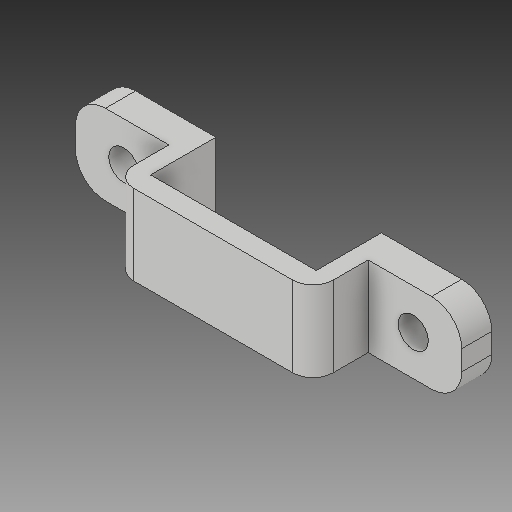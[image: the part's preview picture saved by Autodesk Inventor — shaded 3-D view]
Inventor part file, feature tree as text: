
AUTODESK INVENTOR PART (.ipt)
format: ipt  version: 2018 (Build 220112000, 112)  size: 176,128 bytes
history: native  units: in
note: dims shown in document units (in); Inventor stores cm internally (conversion verified against a paired STEP export)
features: extrude x5, sketch x5, fillet x2, shell x1
ambient origin geometry x8: Origin, YZ Plane, XZ Plane, XY Plane, X Axis, Y Axis, Z Axis, Center Point
bodies: Solid1 (feature_tree)
feature tree (13):
  extrude  "Extrusion1"  Depth=0.6496in
  shell  "Shell1"  Thickness=0.2559in
  extrude  "Extrusion2"  TaperAngle=0.0deg  [1 undecoded]
  extrude  "Extrusion3"  Depth=0.315in
  fillet  "Fillet1"  [1 undecoded]
  extrude  "Extrusion4"  Depth=0.315in
  extrude  "Extrusion6"  Depth=0.0787in
  fillet  "Fillet3"  Radius=0.5679in
  sketch  "Sketch1"  dims[d0=0.315in d1=0.6496in d2=0.2559in d3=0.0in]
  sketch  "Sketch2"  dims[d4=0.1181in d5=0.0in]
  sketch  "Sketch3"  dims[d6=0.315in d7=0.315in d8=0.0in]
  sketch  "Sketch4"  dims[d9=0.315in d10=0.315in]
  sketch  "Sketch6"  dims[d11=0.1181in d12=0.0in d13=1.1358in d14=0.5679in d15=0.5679in d16=0.1181in d17=0.1181in d18=0.1969in d19=0.0in d20=0.1181in d25=0.3543in d26=0.315in d27=0.315in d28=0.3543in d29=1.0in d30=0.0in d33=0.0394in d34=0.0in d35=0.0787in]
note: 2 required parameter values undecoded (feature->parameter linkage not recoverable at this tier; creation-order binding heuristic only, values carry confidence <= 0.55)
